# Revit family: Lighting_Pendants_Zero_Slizes
name_source: partatom
category: Lighting Fixtures
units: mm (PartAtom-declared; Revit-internal decimal feet)

## family parameters
Always vertical = Yes
Cut with Voids When Loaded = No
Light Source = Yes
OmniClass Number = 23.80.70.00
OmniClass Title = Lighting
Part Type = Normal
Room Calculation Point = No
Round Connector Dimension = Use Diameter
Shared = No
Work Plane-Based = No

## types (2) — shared parameters
AssetType = Fixed
BIMObjectName = Lighting_Pendants_Zero_Slizes
Brand = Zero
Category = Luminaires
Collection = Slizes
Color = Various
Color Filter = 16777215
Designer = Halskov & Dalsgaard 2022
Dimming Lamp Color Temperature Shift = <None>
DurationUnit = Hours
ElectricalDeviceNominalPower = 10
Emit Shape Visible in Rendering = No
Emit from Circle Diameter = 86 mm  [stored 0.282152 ft]
ExpectedLife = 50.000h
Features = LED info: With incorporated LED module or with dimmable LED lightsource included GU10 4,9W/2700K, 6,2W/3000K. Module-System power: 11W. Luminaire Luminous Flux: 884LM. CCT 3000K. SDCM 3. CRI 90. L70/50000H
Installation: On ceiling-hook. Including ceiling cup.
Connection: DCL plug or terminalblock 3x4 mm2. When DALI 5x4mm2.
Finish = Painted metal in black RAL 9005. Sound absorbing slices made of polyester and bi-component fibre. Fabric Hush/Gabriel.
HasProtectiveEarth = Yes
IP_Code = IP 20
IfcExportAs = IfcLightFixtureType
IfcExportType = NOTDEFINED
LensMaterial = Mat Acrylic
LightFixtureMainMaterial = Black RAL 9005
LightFixtureMountingType = Suspended
LightFixturePlacingType = Ceilling
Manufacturer = Zero
ManufacturerName = Zero
ManufacturerURL = https://www.zerolighting.com
Material = Metal & textile
NBSDescription = General purpose luminaires
NBSReference = 90-60-50/405
Name = Zero_Slizes
NominalFrequencyRange = 50 Hz
NominalHeight = 416 mm
NominalLength = 580 mm  [stored 1.90289 ft]
NominalVoltage = 230 V
NominalVoltageCalc = 230 V
NominalWidth = 580 mm  [stored 1.90289 ft]
NumberOfPoles = 1
Photometric Web File = Slice_LED.IES
ProductDatasheet = https://www.zerolighting.com
Revision = 1
Shape = Sculptured
Size = 580x580x415 mm
Tilt Angle = 90.00°
TotalWattage = 10 W
URL = https://www.zerolighting.com
Uniclass2 = Pr_70_70_49_43
Uniclass2015Description = Light-emitting diode (LED) luminaires
Uniclass2015Reference = Pr_70_70_48_46
Version = 2
VersionDate = 31/08/2023
zero-valued in all types: Default Elevation, DefaultElevation, NumberOfSources

## per-type parameters (varying)
| type | Article Number | ModelNumber |
| Slizes - Black 11W/884LM On/Off | 12120106-30 | 12120106-30 |
| Slizes - Black 11W/884LM DALI | 12120106D30 | 12120106D30 |

note: column(s) folded — value = type name in every type: Model

note: [stored X ft] marks values corroborated as IEEE doubles in the binary element streams (Revit-internal decimal feet)

## geometry (parser evidence)
native form markers: Sweep x12
no freeform markers — native parametric forms only
